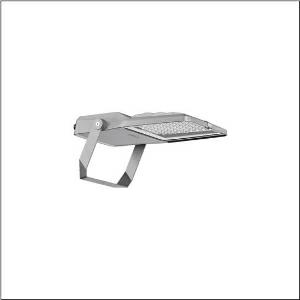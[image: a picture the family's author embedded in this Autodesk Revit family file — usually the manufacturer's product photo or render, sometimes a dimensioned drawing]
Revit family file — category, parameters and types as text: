
# Revit family: floodlight_fl_21_iq_mini___pl52_5xa7772d3d1a_25a1
name_source: partatom
category: Lighting Fixtures
units: mm (PartAtom-declared; Revit-internal decimal feet)

## family parameters
Cut with Voids When Loaded = No
Host = Face
Light Source = No
Part Type = Normal
Room Calculation Point = No
Round Connector Dimension = Use Diameter
Shared = No

## types (1)
- --- (1 x LED, 15340 lm, 143 W, 3000K)
    Apparent Load = 143 VA
    CIE Flux Codes = 26 60 98 100 100
    Color Rendering = 80
    Color Temperature = 3000K
    Default Elevation = 1800 mm
    Description = Floodlight FL 21 iQ mini, floodlight, primary light control with lens, of PMMA, primary optical cover: protective disc, of toughened safety glass, transparent, light distribution: PL52, light emission: direct distribution, installation type: surface-mounted, lamps: LED, High Power LED, rated values: 15.340lm | 143W | 107,3lm/W (begin service life); end service life: 15.340lm | 151,6W; at 50% lumin. flux: 7.670lm | 60,5W | 126,8lm/W, colour temperature: 3000K, colour rendering: CRI > 80, light colour: 830, light setting 1 begin service life: 100% | 15.340lm | 143W | 107,3lm/W | 3.000K, light setting 1 end service life: 151,6W, further light settings possible, control: Street-Remote, Auto-Match, Temp-Guard, Night-Set, Smart-Wire, Desk-Remote (wireless, voltage-free reading and setting of iQ features in the workshop via application-optimized NFC function/RFID function), optimised constant luminous flux control (CLO 2.0), pre-setting: linear dimming characteristic, with terminal, 6-pole, mains connection: 220..240V, AC, 50/60Hz, luminaire housing, of diecast aluminium, powder-coated, SITECO metallic grey (DB 702S), corrosivity category C5 mid according to DIN EN ISO 12944suitable for swimming poolschlorine-resistant, sealing non-destructively replaceable, mounting bracket, of steel, galvanised, powder-coated, SITECO metallic grey (DB 702S), protection rating (complete): IP66, insulation class (complete): insulation class II (safety insulation), certification: CE, ENEC, VDE, protection symbol: D, impact resistance: IK08, permissible operating ambient temperature: -40..+40°C, permissible operating ambient temperature for outdoor applications: -40..+50°C, standard: DIN EN 12944, LABS conformity tested according to VDMA 24364:2018-05, packaging unit: 1 piece

Light Distribution: PL52
    Height = 70 mm
    Lamp = 1 x LED
    Lamp Light Flux = 15340 lm
    Lamp Power = 143 W
    Lamp count = 1
    Length = 485 mm
    Luminous efficacy = 107 lm/W
    Manufacturer = Siteco
    ModVariant = No
    Model = 5XA7772D3D1A
    Number of Poles = 1
    OnlyDefault = Yes
    Power Factor = 1
    Product Name = Floodlight FL 21 iQ mini | PL52
    Product group = floodlight | pylon annexe
    ProductGroupID = 6201
    Protection Class = Protection class II
    Protection Degree = IP 66
    RLX_Detail_Level = 1
    RLX_Emergency_Light_Flux = 0 lm
    RLX_Emergency_Type = 0
    RLX_Emergency_Type_DB = No
    RlxData = <blob elided: 96957 chars, md5=1c8068b0>
    Socket = socket
    Standby Power = 0 W
    System Light Flux = 15340 lm
    System Power = 143 W
    Type Comments = factory setting: luminous flux: 100 % | dim-lin: 254 | 730 mA
    Type Image = l_1006845.jpg
    URL = http://relux.com
    VarID = @adj_163143
    Voltage = 0 V
    Weight = 0.00 kg
    Width = 337 mm

## geometry (parser evidence)
native form markers: Blend x4, Sweep x13
no freeform markers — native parametric forms only
